# Revit family: CL
name_source: partatom
category: Lighting Fixtures
revit_build: Autodesk Revit MEP 2012 (Build: 20110309_2315(x64)
units: mm (PartAtom-declared; Revit-internal decimal feet)

## types (1)
- CL
    Apparent Load = 50 VA
    Connector Description = Lighting Connector
    Default Elevation = 48 "
    Description = The CL series is a recessed, self-contained emergency light
with fully automatic operation suitable for wall or ceiling mount
applications.
    Finish = Finish - Hubbell - White
    Glass = Hubbell- Glass
    Lamp = Halogen lamp
    Load Classification = Lighting
    Manufacturer = Dual-Lite
    Manufacturer Fax = 866-898-0131
    Model = CL
    Product Documentation Link = http://cdn.dual-lite.com
    Product Material = Finish - Hubbell - Steel
    Product Page URL = http://www.dual-lite.com
    URL = http://www.dual-lite.com
    Voltage = 120 V
    Wattage Comments = 12-75 Watt

## geometry (parser evidence)
native form markers: Blend x1, Sweep x5
no freeform markers — native parametric forms only
